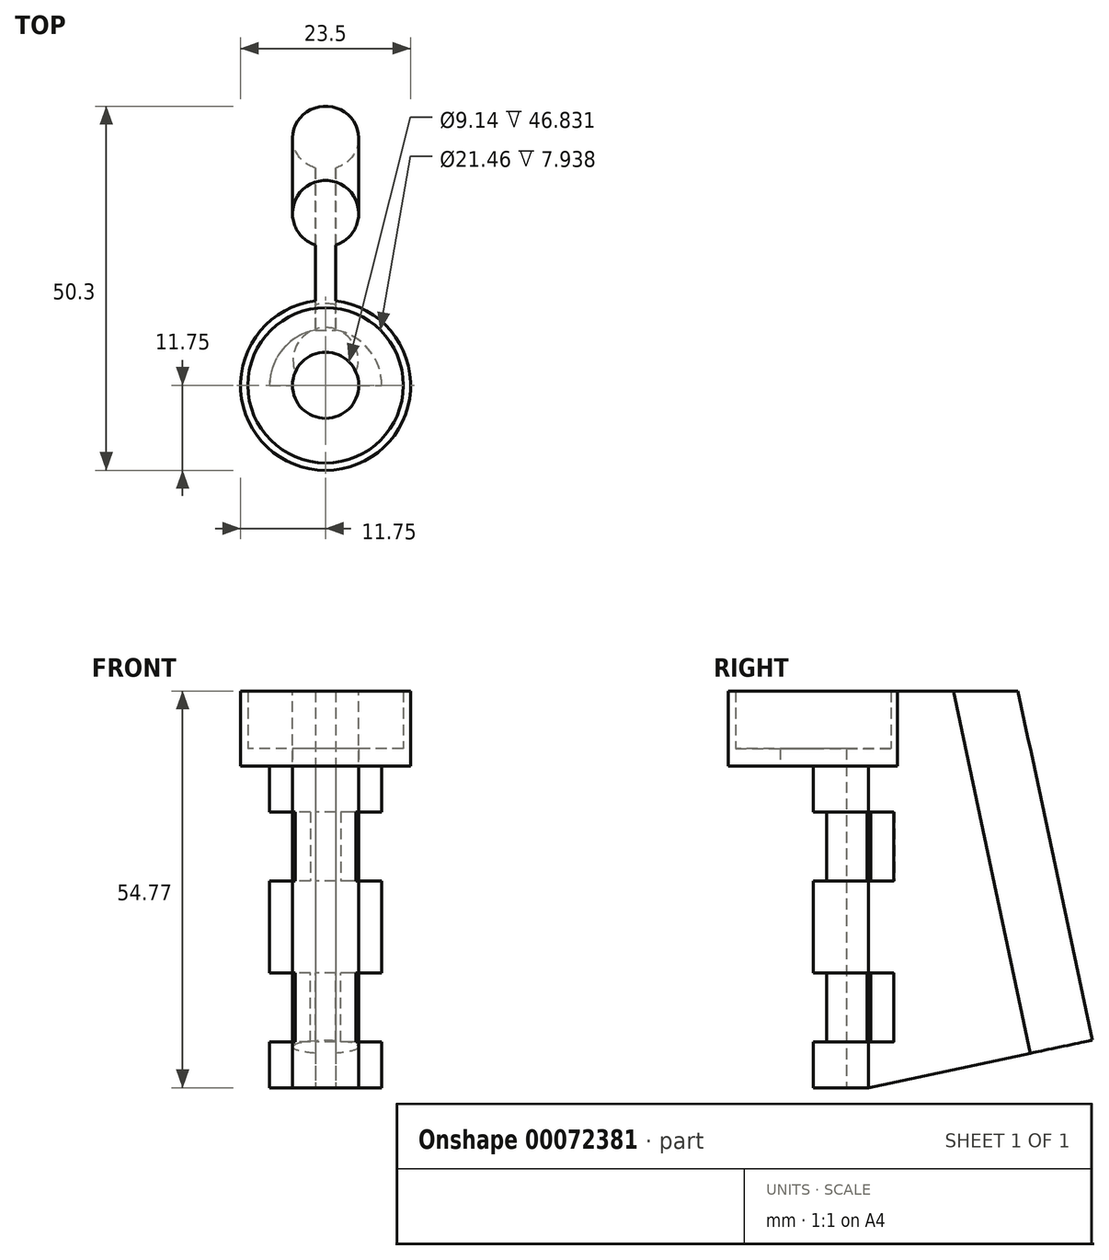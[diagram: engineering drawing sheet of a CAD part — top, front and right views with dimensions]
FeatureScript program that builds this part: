
annotation { "Feature Type Name" : "Feature", "Feature Type Description" : "" }
export const myFeature = defineFeature(function(context is Context, id is Id, definition is map)
    precondition{}
    {
        {
            var Q0;
            Q0=qCreatedBy(makeId("Top.planeOp"),FACE);
            var sketch = newSketch(context, id + "F0", { "sketchPlane" : qUnion([Q0])});
            skArc(sketch, "E0", {"start": v(4.57, 0) * mm, "mid": v(0, 4.57) * mm, "end": v(-4.57, 0) * mm});
            skArc(sketch, "E1", {"start": v(7.75, 0) * mm, "mid": v(0, 7.75) * mm, "end": v(-7.75, 0) * mm});
            skLineSegment(sketch, "E2", {"start": v(-7.75, 0) * mm, "end": v(-4.57, 0) * mm});
            skLineSegment(sketch, "E3", {"start": v(4.57, 0) * mm, "end": v(7.75, 0) * mm});
            skCircle(sketch, "E4", {"center": v(0, 23.73) * mm, "radius": 4.57 * mm, "construction": true});
            skLineSegment(sketch, "E5.rect.bottom", {"start": v(1.4, 7.62) * mm, "end": v(-1.4, 7.62) * mm, "construction": true});
            skLineSegment(sketch, "E5.rect.top", {"start": v(1.4, 19.38) * mm, "end": v(-1.4, 19.38) * mm});
            skLineSegment(sketch, "E5.rect.left", {"start": v(1.4, 7.62) * mm, "end": v(1.4, 19.38) * mm});
            skLineSegment(sketch, "E5.rect.right", {"start": v(-1.4, 7.62) * mm, "end": v(-1.4, 19.38) * mm});
            skPoint(sketch, "E5.rect.middle", {"position": v(0, 13.5) * mm});
            skSolve(sketch);
        }
        {
            var Q0;
            Q0=qSketchRegion(id+"F0",true);
            extrude(context, id + "F1", {"entities" : qUnion([Q0]), "depth" : 44.45 * mm});
        }
        {
            var Q0;
            Q0=makeQuery(id+"F1.opExtrude","SWEPT_FACE",FACE,{"disambiguationData":[OSD([sQuery(id+"F0.wireOp",EDGE,"E5.rect.left")])]});
            var sketch = newSketch(context, id + "F2", { "sketchPlane" : qUnion([Q0])});
            skLineSegment(sketch, "E6.bottom", {"start": v(7.62, 3.18) * mm, "end": v(10.8, 3.18) * mm});
            skLineSegment(sketch, "E6.top", {"start": v(7.62, 12.7) * mm, "end": v(10.8, 12.7) * mm});
            skLineSegment(sketch, "E6.left", {"start": v(7.62, 3.17) * mm, "end": v(7.62, 12.7) * mm});
            skLineSegment(sketch, "E6.right", {"start": v(10.8, 3.18) * mm, "end": v(10.8, 12.7) * mm});
            skLineSegment(sketch, "E7.bottom", {"start": v(7.62, 31.75) * mm, "end": v(10.8, 31.75) * mm});
            skLineSegment(sketch, "E7.top", {"start": v(7.62, 41.28) * mm, "end": v(10.8, 41.28) * mm});
            skLineSegment(sketch, "E7.left", {"start": v(7.62, 31.75) * mm, "end": v(7.62, 41.28) * mm});
            skLineSegment(sketch, "E7.right", {"start": v(10.8, 31.75) * mm, "end": v(10.8, 41.28) * mm});
            skLineSegment(sketch, "E8", {"start": v(10.8, 41.28) * mm, "end": v(10.8, 44.45) * mm, "construction": true});
            skLineSegment(sketch, "E9", {"start": v(10.8, 3.18) * mm, "end": v(10.8, 0) * mm, "construction": true});
            skLineSegment(sketch, "E10.rect.bottom", {"start": v(2.38, 41.28) * mm, "end": v(-2.38, 41.28) * mm});
            skLineSegment(sketch, "E10.rect.top", {"start": v(2.38, 31.75) * mm, "end": v(-2.38, 31.75) * mm});
            skLineSegment(sketch, "E10.rect.left", {"start": v(2.38, 41.28) * mm, "end": v(2.38, 31.75) * mm});
            skLineSegment(sketch, "E10.rect.right", {"start": v(-2.38, 41.28) * mm, "end": v(-2.38, 31.75) * mm});
            skPoint(sketch, "E10.rect.middle", {"position": v(0, 36.51) * mm});
            skLineSegment(sketch, "E11.rect.bottom", {"start": v(2.38, 3.17) * mm, "end": v(-2.38, 3.17) * mm});
            skLineSegment(sketch, "E11.rect.top", {"start": v(2.38, 12.7) * mm, "end": v(-2.38, 12.7) * mm});
            skLineSegment(sketch, "E11.rect.left", {"start": v(2.38, 3.18) * mm, "end": v(2.38, 12.7) * mm});
            skLineSegment(sketch, "E11.rect.right", {"start": v(-2.38, 3.18) * mm, "end": v(-2.38, 12.7) * mm});
            skPoint(sketch, "E11.rect.middle", {"position": v(0, 7.94) * mm});
            skSolve(sketch);
        }
        {
            var Q0;
            Q0=qCreatedBy(makeId("Top.planeOp"),FACE);
            var sketch = newSketch(context, id + "F3", { "sketchPlane" : qUnion([Q0])});
            skCircle(sketch, "E12", {"center": v(0, 1.78) * mm, "radius": 2.8 * mm, "construction": true});
            skLineSegment(sketch, "E13", {"start": v(-2.68, 4.57) * mm, "end": v(4.01, 4.57) * mm, "construction": true});
            skLineSegment(sketch, "E14", {"start": v(-3.3, -1.02) * mm, "end": v(3.4, -1.02) * mm, "construction": true});
            skCircle(sketch, "E15", {"center": v(0, 3.48) * mm, "radius": 4.5 * mm});
            skCircle(sketch, "E16", {"center": v(0, 3.48) * mm, "radius": 7.8 * mm});
            skLineSegment(sketch, "E17.bottom", {"start": v(-8.86, 1.25) * mm, "end": v(11.53, 1.25) * mm});
            skLineSegment(sketch, "E17.top", {"start": v(-8.86, -6.45) * mm, "end": v(11.53, -6.45) * mm});
            skLineSegment(sketch, "E17.left", {"start": v(-8.86, 1.25) * mm, "end": v(-8.86, -6.45) * mm});
            skLineSegment(sketch, "E17.right", {"start": v(11.53, 1.25) * mm, "end": v(11.53, -6.45) * mm});
            skSolve(sketch);
        }
        {
            var Q0;
            Q0=qCreatedBy(makeId("Top.planeOp"),FACE);
            var Q1;
            Q1=makeQuery(id+"F1.opExtrude","CAP_FACE",FACE,{"disambiguationData":[OSD([sQuery(id+"F0.wireOp",EDGE,"E0"),sQuery(id+"F0.wireOp",EDGE,"E1"),sQuery(id+"F0.wireOp",EDGE,"E2"),sQuery(id+"F0.wireOp",EDGE,"E3"),sQuery(id+"F0.wireOp",EDGE,"E4"),sQuery(id+"F0.wireOp",EDGE,"E5.rect.left"),sQuery(id+"F0.wireOp",EDGE,"E5.rect.right")])],"isStart":false});
            cPlane(context, id + "F4", {"entities" : qUnion([Q0, Q1]), "cplaneType" : CPlaneType.MID_PLANE, "offset" : 152.4 * mm, "width" : 152.4 * mm, "height" : 152.4 * mm});
        }
        {
            var Q0;
            Q0=qCreatedBy(id+"F4.planeOp",FACE);
            cPlane(context, id + "F5", {"entities" : qUnion([Q0]), "cplaneType" : CPlaneType.OFFSET, "offset" : 6.35 * mm, "width" : 152.4 * mm, "height" : 152.4 * mm});
        }
        {
            var Q0;
            Q0=qCreatedBy(id+"F5.planeOp",FACE);
            var sketch = newSketch(context, id + "F6", { "sketchPlane" : qUnion([Q0])});
            skCircle(sketch, "E18", {"center": v(0, 3.48) * mm, "radius": 4.5 * mm});
            skCircle(sketch, "E19", {"center": v(0, 3.48) * mm, "radius": 7.8 * mm});
            skLineSegment(sketch, "E20.bottom", {"start": v(-8.42, 1.76) * mm, "end": v(11.76, 1.76) * mm});
            skLineSegment(sketch, "E20.top", {"start": v(-8.42, -6.32) * mm, "end": v(11.76, -6.32) * mm});
            skLineSegment(sketch, "E20.left", {"start": v(-8.42, 1.76) * mm, "end": v(-8.42, -6.32) * mm});
            skLineSegment(sketch, "E20.right", {"start": v(11.76, 1.76) * mm, "end": v(11.76, -6.32) * mm});
            skSolve(sketch);
        }
        {
            var Q0;
            Q0=qCreatedBy(id+"F4.planeOp",FACE);
            cPlane(context, id + "F7", {"entities" : qUnion([Q0]), "cplaneType" : CPlaneType.OFFSET, "offset" : 6.35 * mm, "oppositeDirection" : true, "width" : 152.4 * mm, "height" : 152.4 * mm});
        }
        {
            var Q0;
            Q0=qCreatedBy(id+"F7.planeOp",FACE);
            var sketch = newSketch(context, id + "F8", { "sketchPlane" : qUnion([Q0])});
            skCircle(sketch, "E21", {"center": v(0, 3.48) * mm, "radius": 4.5 * mm});
            skCircle(sketch, "E22", {"center": v(0, 3.48) * mm, "radius": 7.8 * mm});
            skLineSegment(sketch, "E23.bottom", {"start": v(-8.58, 1.82) * mm, "end": v(8.4, 1.82) * mm});
            skLineSegment(sketch, "E23.top", {"start": v(-8.58, -6) * mm, "end": v(8.4, -6) * mm});
            skLineSegment(sketch, "E23.left", {"start": v(-8.58, 1.82) * mm, "end": v(-8.58, -6) * mm});
            skLineSegment(sketch, "E23.right", {"start": v(8.4, 1.82) * mm, "end": v(8.4, -6) * mm});
            skSolve(sketch);
        }
        {
            var Q0;
            Q0=makeQuery(id+"F6.imprint","IMPRINT",FACE,{"disambiguationData":[TD([[makeQuery(id+"F6.imprint","IMPRINT",EDGE,{"derivedFrom":sQuery(id+"F6.wireOp",EDGE,"E18")}),-1.0]])]});
            var Q1;
            Q1=makeQuery(id+"F6.imprint","IMPRINT",FACE,{"disambiguationData":[TD([[makeQuery(id+"F6.imprint","IMPRINT",EDGE,{"derivedFrom":sQuery(id+"F6.wireOp",EDGE,"E20.top")}),1.0]])]});
            extrude(context, id + "F9", {"entities" : qUnion([Q0, Q1]), "operationType" : NewBodyOperationType.REMOVE, "depth" : 9.52 * mm});
        }
        {
            var Q0;
            Q0=makeQuery(id+"F8.imprint","IMPRINT",FACE,{"disambiguationData":[TD([[makeQuery(id+"F8.imprint","IMPRINT",EDGE,{"derivedFrom":sQuery(id+"F8.wireOp",EDGE,"E21")}),-1.0]])]});
            var Q1;
            Q1=makeQuery(id+"F8.imprint","IMPRINT",FACE,{"disambiguationData":[TD([[makeQuery(id+"F8.imprint","IMPRINT",EDGE,{"derivedFrom":sQuery(id+"F8.wireOp",EDGE,"E23.top")}),1.0]])]});
            extrude(context, id + "F10", {"entities" : qUnion([Q0, Q1]), "operationType" : NewBodyOperationType.REMOVE, "oppositeDirection" : true, "depth" : 9.52 * mm});
        }
        {
            var Q0;
            Q0=makeQuery(id+"F1.opExtrude","CAP_FACE",FACE,{"disambiguationData":[OSD([sQuery(id+"F0.wireOp",EDGE,"E0"),sQuery(id+"F0.wireOp",EDGE,"E1"),sQuery(id+"F0.wireOp",EDGE,"E2"),sQuery(id+"F0.wireOp",EDGE,"E3"),sQuery(id+"F0.wireOp",EDGE,"E4"),sQuery(id+"F0.wireOp",EDGE,"E5.rect.left"),sQuery(id+"F0.wireOp",EDGE,"E5.rect.right")])],"isStart":false});
            var sketch = newSketch(context, id + "F11", { "sketchPlane" : qUnion([Q0])});
            skCircle(sketch, "E24", {"center": v(0, 0) * mm, "radius": 11.75 * mm});
            skCircle(sketch, "E25", {"center": v(0, 0) * mm, "radius": 4.57 * mm});
            skSolve(sketch);
        }
        {
            var Q0;
            {var subQ0=sQuery(id+"F0.wireOp",EDGE,"E2");var subQ9=makeQuery(id+"F1.opExtrude","CAP_EDGE",EDGE,{"disambiguationData":[OSD([subQ0])],"isStart":false});Q0=makeQuery(id+"F11.imprint","IMPRINT",FACE,{"disambiguationData":[TD([[makeQuery(id+"F11.imprint","IMPRINT",EDGE,{"derivedFrom":subQ9}),-1.0]])]});}
            var Q1;
            {var subQ0=sQuery(id+"F0.wireOp",EDGE,"E2");var subQ9=makeQuery(id+"F1.opExtrude","CAP_EDGE",EDGE,{"disambiguationData":[OSD([subQ0])],"isStart":false});Q1=makeQuery(id+"F11.imprint","IMPRINT",FACE,{"disambiguationData":[TD([[makeQuery(id+"F11.imprint","IMPRINT",EDGE,{"derivedFrom":subQ9}),1.0]])]});}
            extrude(context, id + "F12", {"entities" : qUnion([Q0, Q1]), "operationType" : NewBodyOperationType.ADD, "depth" : 2.38 * mm});
        }
        {
            var Q0;
            Q0=makeQuery(id+"F12.opExtrude","CAP_FACE",FACE,{"disambiguationData":[OSD([sQuery(id+"F11.wireOp",EDGE,"E24"),sQuery(id+"F11.wireOp",EDGE,"E25")])],"isStart":false});
            var sketch = newSketch(context, id + "F13", { "sketchPlane" : qUnion([Q0])});
            skCircle(sketch, "E26", {"center": v(0, 0) * mm, "radius": 11.75 * mm});
            skCircle(sketch, "E27", {"center": v(0, 0) * mm, "radius": 10.73 * mm});
            skSolve(sketch);
        }
        {
            var Q0;
            Q0=qSketchRegion(id+"F13",true);
            extrude(context, id + "F14", {"entities" : qUnion([Q0]), "operationType" : NewBodyOperationType.ADD, "depth" : 7.94 * mm});
        }
        {
            var Q0;
            Q0=makeQuery(id+"F1.opExtrude","CAP_FACE",FACE,{"disambiguationData":[OSD([sQuery(id+"F0.wireOp",EDGE,"E0"),sQuery(id+"F0.wireOp",EDGE,"E1"),sQuery(id+"F0.wireOp",EDGE,"E2"),sQuery(id+"F0.wireOp",EDGE,"E3"),sQuery(id+"F0.wireOp",EDGE,"E4"),sQuery(id+"F0.wireOp",EDGE,"E5.rect.left"),sQuery(id+"F0.wireOp",EDGE,"E5.rect.right")])],"isStart":false});
            var Q1;
            Q1=makeQuery(id+"F14.opExtrude","CAP_FACE",FACE,{"disambiguationData":[OSD([sQuery(id+"F13.wireOp",EDGE,"E26"),sQuery(id+"F13.wireOp",EDGE,"E27")])],"isStart":false});
            extrude(context, id + "F15", {"entities" : qUnion([Q0]), "operationType" : NewBodyOperationType.ADD, "endBound" : BoundingType.UP_TO_SURFACE, "endBoundEntityFace" : qUnion([Q1]), "depth" : 25.4 * mm});
        }
        {
            var Q0;
            Q0=makeQuery(id+"F15.boolean.opBoolean","MERGE",FACE,{"derivedFrom":[makeQuery(id+"F14.opExtrude","CAP_FACE",FACE,{"disambiguationData":[OSD([sQuery(id+"F13.wireOp",EDGE,"E26"),sQuery(id+"F13.wireOp",EDGE,"E27")])],"isStart":false}),makeQuery(id+"F15.opExtrude","CAP_FACE",FACE,{"disambiguationData":[OSD([sQuery(id+"F0.wireOp",EDGE,"E0"),sQuery(id+"F0.wireOp",EDGE,"E1"),sQuery(id+"F0.wireOp",EDGE,"E2"),sQuery(id+"F0.wireOp",EDGE,"E3"),sQuery(id+"F0.wireOp",EDGE,"E5.rect.top"),sQuery(id+"F0.wireOp",EDGE,"E5.rect.left"),sQuery(id+"F0.wireOp",EDGE,"E5.rect.right")])],"isStart":false})]});
            var sketch = newSketch(context, id + "F16", { "sketchPlane" : qUnion([Q0])});
            skCircle(sketch, "E28", {"center": v(0, 23.73) * mm, "radius": 4.57 * mm});
            skPoint(sketch, "E28.centerSnap0", {"position": v(0, 19.38) * mm});
            skSolve(sketch);
        }
        {
            var Q0;
            Q0=qCreatedBy(makeId("Right.planeOp"),FACE);
            var sketch = newSketch(context, id + "F17", { "sketchPlane" : qUnion([Q0])});
            skLineSegment(sketch, "E29", {"start": v(23.73, 54.77) * mm, "end": v(23.73, 24.03) * mm, "construction": true});
            skLineSegment(sketch, "E30", {"start": v(23.73, 54.77) * mm, "end": v(35.37, 0) * mm});
            skLineSegment(sketch, "E31", {"start": v(35.37, 0) * mm, "end": v(19.38, 0) * mm, "construction": true});
            skSolve(sketch);
        }
        {
            var Q0;
            {var subQ1=makeQuery(id+"F15.opExtrude","CAP_EDGE",EDGE,{"disambiguationData":[OSD([sQuery(id+"F0.wireOp",EDGE,"E5.rect.top")])],"isStart":false});Q0=makeQuery(id+"F16.imprint","IMPRINT",FACE,{"disambiguationData":[TD([[makeQuery(id+"F16.imprint","IMPRINT",EDGE,{"derivedFrom":subQ1}),-1.0]])]});}
            var Q1;
            Q1=sQuery(id+"F17.wireOp",EDGE,"E30");
            sweep(context, id + "F18", {"profiles" : qUnion([Q0]), "path" : qUnion([Q1])});
        }
        {
            var Q0;
            {var subQ0=sQuery(id+"F0.wireOp",EDGE,"E5.rect.top");Q0=makeQuery(id+"F15.boolean.opBoolean","MERGE",FACE,{"derivedFrom":[makeQuery(id+"F1.opExtrude","SWEPT_FACE",FACE,{"disambiguationData":[OSD([subQ0])]}),makeQuery(id+"F15.opExtrude","SWEPT_FACE",FACE,{"disambiguationData":[OSD([subQ0])]})]});}
            extrude(context, id + "F19", {"entities" : qUnion([Q0]), "endBound" : BoundingType.UP_TO_NEXT, "depth" : 25.4 * mm});
        }
        {
            var Q0;
            Q0=makeQuery(id+"F1.opExtrude","SWEPT_BODY",BODY,{"disambiguationData":[OSD([sQuery(id+"F0.wireOp",EDGE,"E0"),sQuery(id+"F0.wireOp",EDGE,"E1"),sQuery(id+"F0.wireOp",EDGE,"E2"),sQuery(id+"F0.wireOp",EDGE,"E3"),sQuery(id+"F0.wireOp",EDGE,"E5.rect.top"),sQuery(id+"F0.wireOp",EDGE,"E5.rect.left"),sQuery(id+"F0.wireOp",EDGE,"E5.rect.right")])]});
            var Q1;
            Q1=makeQuery(id+"F18.opSweep","SWEPT_BODY",BODY,{"disambiguationData":[OSD([sQuery(id+"F0.wireOp",EDGE,"E5.rect.top"),sQuery(id+"F16.wireOp",EDGE,"E28"),sQuery(id+"F17.wireOp",EDGE,"E30")])]});
            var Q2;
            Q2=makeQuery(id+"F19.opExtrude","SWEPT_BODY",BODY,{"disambiguationData":[OSD([sQuery(id+"F0.wireOp",EDGE,"E5.rect.top")])]});
            booleanBodies(context, id + "F20", {"operationType" : BooleanOperationType.UNION, "tools" : qUnion([Q0, Q1, Q2])});
        }
        {
            var Q0;
            Q0=qCreatedBy(makeId("Right.planeOp"),FACE);
            var sketch = newSketch(context, id + "F21", { "sketchPlane" : qUnion([Q0])});
            skLineSegment(sketch, "E32", {"start": v(22.81, 38.62) * mm, "end": v(32.25, -5.79) * mm, "construction": true});
            skLineSegment(sketch, "E33", {"start": v(7.62, 0) * mm, "end": v(39.64, 6.8) * mm});
            skLineSegment(sketch, "E34", {"start": v(39.64, 6.8) * mm, "end": v(41.57, -2.25) * mm});
            skLineSegment(sketch, "E35", {"start": v(41.57, -2.25) * mm, "end": v(8.25, -2.25) * mm});
            skLineSegment(sketch, "E36", {"start": v(8.25, -2.25) * mm, "end": v(7.62, 0) * mm});
            skSolve(sketch);
        }
        {
            var Q0;
            Q0=makeQuery(id+"F21.imprint","IMPRINT",FACE,{"disambiguationData":[TD([[makeQuery(id+"F21.imprint","IMPRINT",EDGE,{"derivedFrom":sQuery(id+"F21.wireOp",EDGE,"E33")}),-1.0]])]});
            extrude(context, id + "F22", {"entities" : qUnion([Q0]), "operationType" : NewBodyOperationType.REMOVE, "endBound" : BoundingType.SYMMETRIC, "oppositeDirection" : true, "depth" : 25.4 * mm});
        }
    });
